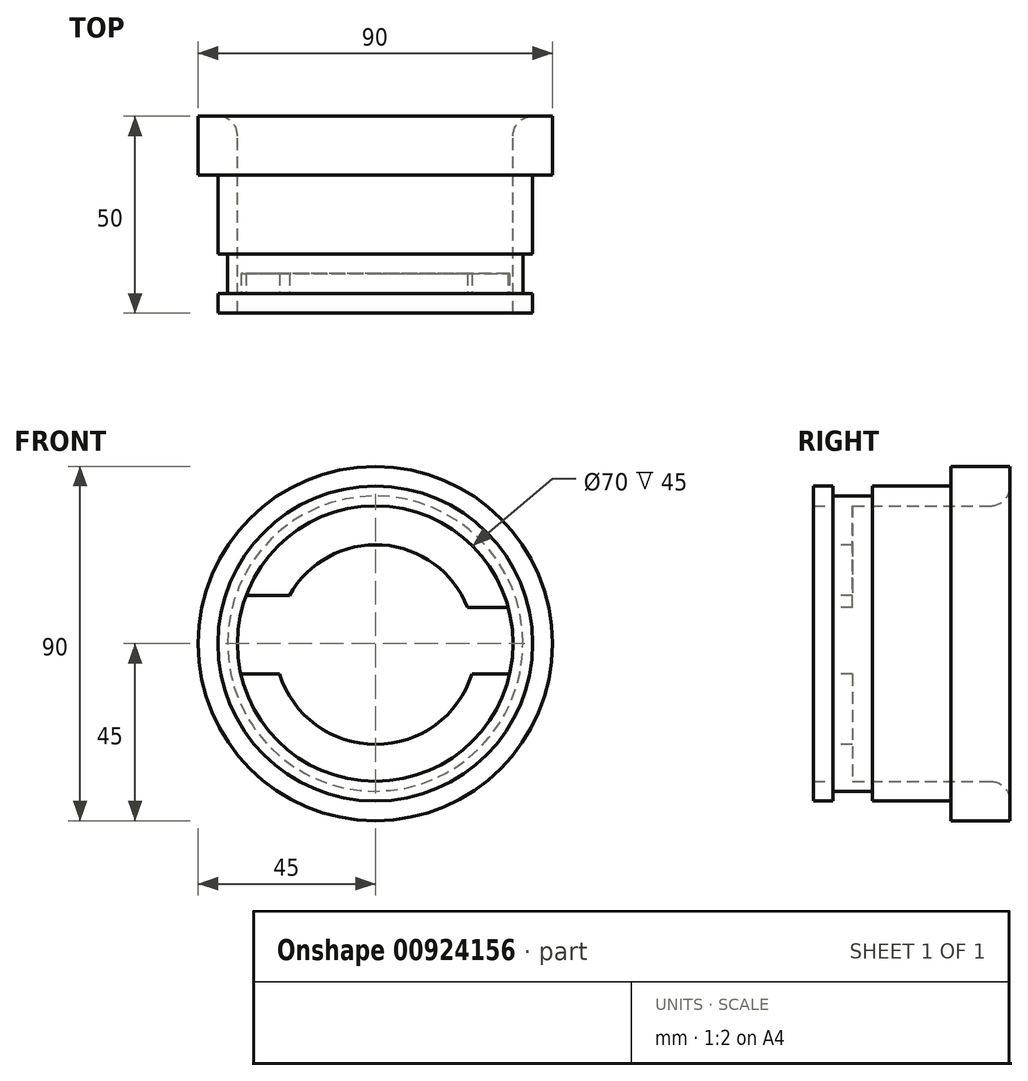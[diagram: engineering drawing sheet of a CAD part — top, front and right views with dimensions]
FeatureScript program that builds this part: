
annotation { "Feature Type Name" : "Feature", "Feature Type Description" : "" }
export const myFeature = defineFeature(function(context is Context, id is Id, definition is map)
    precondition{}
    {
        {
            var Q0;
            Q0=qCreatedBy(makeId("Front.planeOp"),FACE);
            var sketch = newSketch(context, id + "F0", { "sketchPlane" : qUnion([Q0])});
            skCircle(sketch, "E0", {"center": v(0, 0) * mm, "radius": 35 * mm});
            skCircle(sketch, "E1", {"center": v(0, 0) * mm, "radius": 40 * mm});
            skSolve(sketch);
        }
        {
            var Q0;
            Q0=makeQuery(id+"F0.imprint","IMPRINT",FACE,{"disambiguationData":[TD([[makeQuery(id+"F0.imprint","IMPRINT",EDGE,{"derivedFrom":sQuery(id+"F0.wireOp",EDGE,"E0")}),-1.0]])]});
            extrude(context, id + "F1", {"entities" : qUnion([Q0]), "depth" : 50 * mm, "offsetDistance" : 25 * mm});
        }
        {
            var Q0;
            Q0=qCreatedBy(makeId("Front.planeOp"),FACE);
            var sketch = newSketch(context, id + "F2", { "sketchPlane" : qUnion([Q0])});
            skCircle(sketch, "E2", {"center": v(0, 0) * mm, "radius": 35 * mm});
            skCircle(sketch, "E3", {"center": v(0, 0) * mm, "radius": 45 * mm});
            skSolve(sketch);
        }
        {
            var Q0;
            Q0 = qSketchRegion(id + "F2", true);
            extrude(context, id + "F3", {"entities" : qUnion([Q0]), "operationType" : NewBodyOperationType.ADD, "depth" : 15 * mm, "offsetDistance" : 25 * mm});
        }
        {
            var Q0;
            Q0=makeQuery(id+"F1.opExtrude","CAP_EDGE",EDGE,{"disambiguationData":[OSD([sQuery(id+"F0.wireOp",EDGE,"E0")])],"isStart":true});
            fillet(context, id + "F4", {"entities" : qUnion([Q0]), "radius" : 5 * mm, "tangentPropagation" : true, "allowEdgeOverflow" : false});
        }
        {
            var Q0;
            Q0=qCreatedBy(makeId("Front.planeOp"),FACE);
            cPlane(context, id + "F5", {"entities" : qUnion([Q0]), "cplaneType" : CPlaneType.OFFSET, "offset" : 45 * mm, "width" : 150 * mm, "height" : 150 * mm});
        }
        {
            var Q0;
            Q0=qCreatedBy(id+"F5.planeOp",FACE);
            var sketch = newSketch(context, id + "F6", { "sketchPlane" : qUnion([Q0])});
            skCircle(sketch, "E4", {"center": v(0, 0) * mm, "radius": 40 * mm});
            skCircle(sketch, "E5", {"center": v(0, 0) * mm, "radius": 37.5 * mm});
            skSolve(sketch);
        }
        {
            var Q0;
            Q0 = qSketchRegion(id + "F6", true);
            extrude(context, id + "F7", {"entities" : qUnion([Q0]), "operationType" : NewBodyOperationType.REMOVE, "oppositeDirection" : true, "depth" : 10 * mm, "offsetDistance" : 25 * mm});
        }
        {
            var Q0;
            Q0=qCreatedBy(id+"F5.planeOp",FACE);
            var sketch = newSketch(context, id + "F8", { "sketchPlane" : qUnion([Q0])});
            skArc(sketch, "E6", {"start": v(33.76, 9.23) * mm, "mid": v(1.58, 34.96) * mm, "end": v(-32.8, 12.24) * mm});
            skArc(sketch, "E7", {"start": v(23.44, 9.23) * mm, "mid": v(1.77, 25.05) * mm, "end": v(-21.8, 12.24) * mm});
            skLineSegment(sketch, "E8", {"start": v(-32.8, 12.24) * mm, "end": v(-21.8, 12.24) * mm});
            skLineSegment(sketch, "E9", {"start": v(23.44, 9.23) * mm, "end": v(33.76, 9.23) * mm});
            skSolve(sketch);
        }
        {
            var Q0;
            Q0 = qSketchRegion(id + "F8", true);
            extrude(context, id + "F9", {"entities" : qUnion([Q0]), "operationType" : NewBodyOperationType.ADD, "oppositeDirection" : true, "depth" : 5 * mm, "offsetDistance" : 25 * mm});
        }
        {
            var Q0;
            Q0=qCreatedBy(id+"F5.planeOp",FACE);
            var sketch = newSketch(context, id + "F10", { "sketchPlane" : qUnion([Q0])});
            skArc(sketch, "E10", {"start": v(-34.14, -7.7) * mm, "mid": v(0, -35) * mm, "end": v(34.14, -7.7) * mm});
            skArc(sketch, "E11", {"start": v(-24.35, -7.7) * mm, "mid": v(0.1, -25.62) * mm, "end": v(24.56, -7.7) * mm});
            skLineSegment(sketch, "E12", {"start": v(34.14, -7.7) * mm, "end": v(24.56, -7.7) * mm});
            skLineSegment(sketch, "E13", {"start": v(-24.35, -7.7) * mm, "end": v(-34.14, -7.7) * mm});
            skSolve(sketch);
        }
        {
            var Q0;
            Q0 = qSketchRegion(id + "F10", true);
            extrude(context, id + "F11", {"entities" : qUnion([Q0]), "operationType" : NewBodyOperationType.ADD, "oppositeDirection" : true, "depth" : 5 * mm, "offsetDistance" : 25 * mm});
        }
    });
